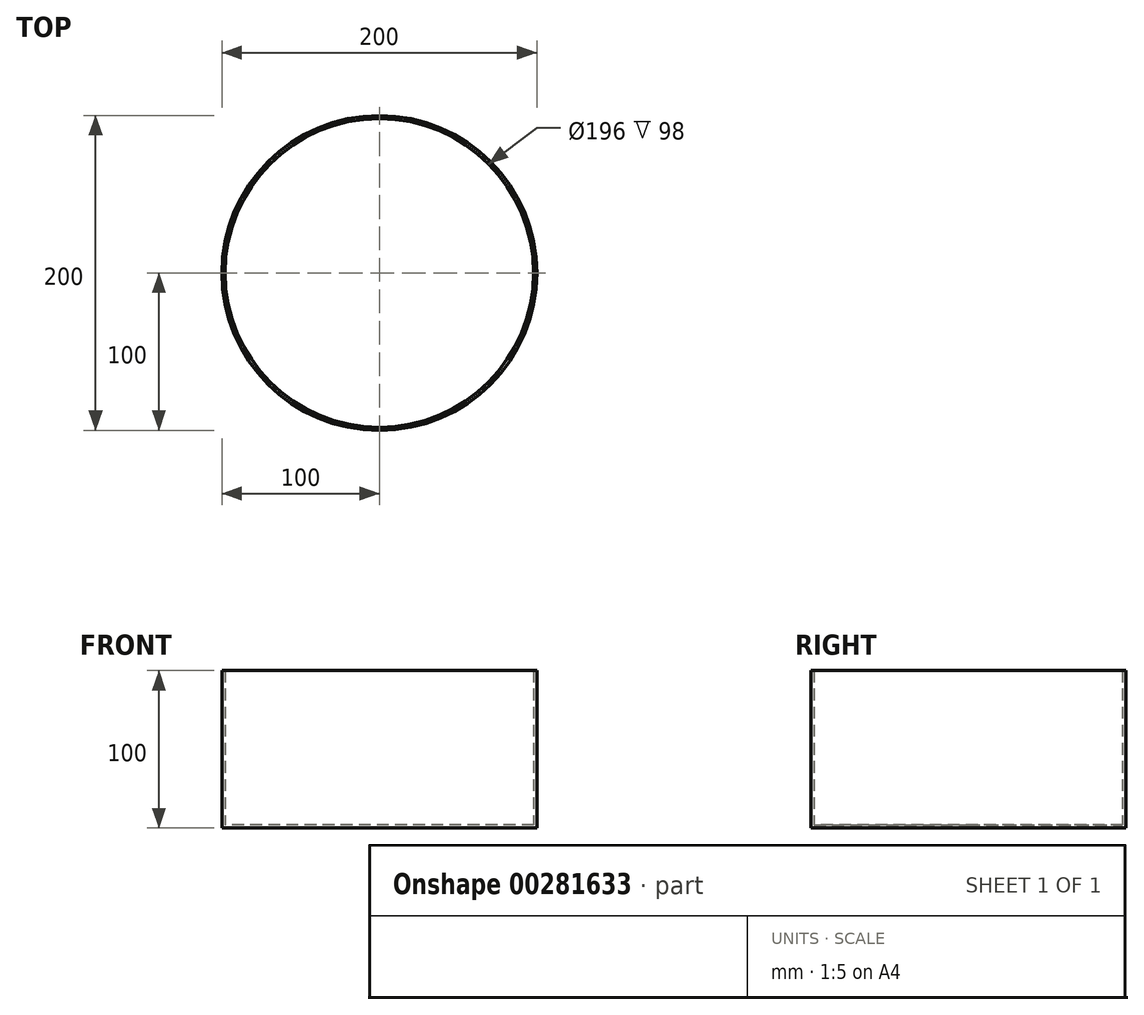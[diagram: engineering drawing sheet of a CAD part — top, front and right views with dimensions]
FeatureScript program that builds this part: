
annotation { "Feature Type Name" : "Feature", "Feature Type Description" : "" }
export const myFeature = defineFeature(function(context is Context, id is Id, definition is map)
    precondition{}
    {
        {
            var Q0;
            Q0=qCreatedBy(makeId("Top.planeOp"),FACE);
            var sketch = newSketch(context, id + "F0", { "sketchPlane" : qUnion([Q0])});
            skCircle(sketch, "E0", {"center": v(0, 0) * mm, "radius": 100 * mm});
            skSolve(sketch);
        }
        {
            var Q0;
            Q0=makeQuery(id+"F0.imprint","IMPRINT",FACE,{"disambiguationData":[TD([[makeQuery(id+"F0.imprint","IMPRINT",EDGE,{"derivedFrom":sQuery(id+"F0.wireOp",EDGE,"E0")}),1.0]])]});
            extrude(context, id + "F1", {"entities" : qUnion([Q0]), "depth" : 100 * mm, "offsetDistance" : 25 * mm});
        }
        {
            var Q0;
            Q0=makeQuery(id+"F1.opExtrude","CAP_FACE",FACE,{"disambiguationData":[OSD([sQuery(id+"F0.wireOp",EDGE,"E0")])],"isStart":false});
            shell(context, id + "F2", {"entities" : qUnion([Q0]), "thickness" : 2 * mm});
        }
    });
